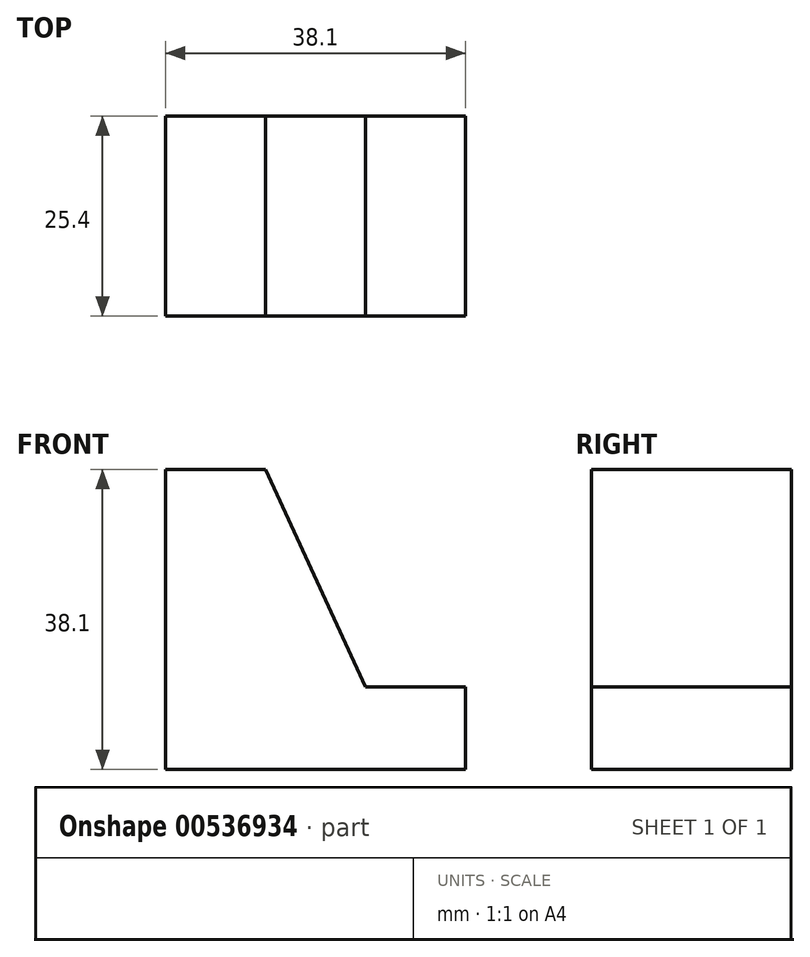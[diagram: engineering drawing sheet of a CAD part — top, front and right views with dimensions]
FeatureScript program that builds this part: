
annotation { "Feature Type Name" : "Feature", "Feature Type Description" : "" }
export const myFeature = defineFeature(function(context is Context, id is Id, definition is map)
    precondition{}
    {
        {
            var Q0;
            Q0=qCreatedBy(makeId("Right.planeOp"),FACE);
            var sketch = newSketch(context, id + "F0", { "sketchPlane" : qUnion([Q0])});
            skLineSegment(sketch, "E0.bottom", {"start": v(-18.4, 0) * mm, "end": v(7, 0) * mm});
            skLineSegment(sketch, "E0.top", {"start": v(-18.4, 38.1) * mm, "end": v(7, 38.1) * mm});
            skLineSegment(sketch, "E0.left", {"start": v(-18.4, 0) * mm, "end": v(-18.4, 38.1) * mm});
            skLineSegment(sketch, "E0.right", {"start": v(7, 0) * mm, "end": v(7, 38.1) * mm});
            skSolve(sketch);
        }
        {
            var Q0;
            Q0=makeQuery(id+"F0.imprint","IMPRINT",FACE,{"disambiguationData":[TD([[makeQuery(id+"F0.imprint","IMPRINT",EDGE,{"derivedFrom":sQuery(id+"F0.wireOp",EDGE,"E0.bottom")}),1.0]])]});
            extrude(context, id + "F1", {"entities" : qUnion([Q0]), "depth" : 38.1 * mm, "offsetDistance" : 25.4 * mm});
        }
        {
            var Q0;
            Q0=makeQuery(id+"F1.opExtrude","SWEPT_FACE",FACE,{"disambiguationData":[OSD([sQuery(id+"F0.wireOp",EDGE,"E0.left")])]});
            var sketch = newSketch(context, id + "F2", { "sketchPlane" : qUnion([Q0])});
            skLineSegment(sketch, "E1", {"start": v(12.7, 38.1) * mm, "end": v(25.4, 10.45) * mm});
            skLineSegment(sketch, "E2", {"start": v(25.4, 10.45) * mm, "end": v(38.1, 10.45) * mm});
            skSolve(sketch);
        }
        {
            var Q0;
            {var subQ0=sQuery(id+"F2.wireOp",EDGE,"E1");Q0=makeQuery(id+"F2.imprint","IMPRINT",FACE,{"disambiguationData":[TD([[makeQuery(id+"F2.imprint","IMPRINT",EDGE,{"derivedFrom":subQ0}),1.0]])]});}
            extrude(context, id + "F3", {"entities" : qUnion([Q0]), "operationType" : NewBodyOperationType.REMOVE, "oppositeDirection" : true, "depth" : 25.4 * mm, "offsetDistance" : 25.4 * mm});
        }
    });
